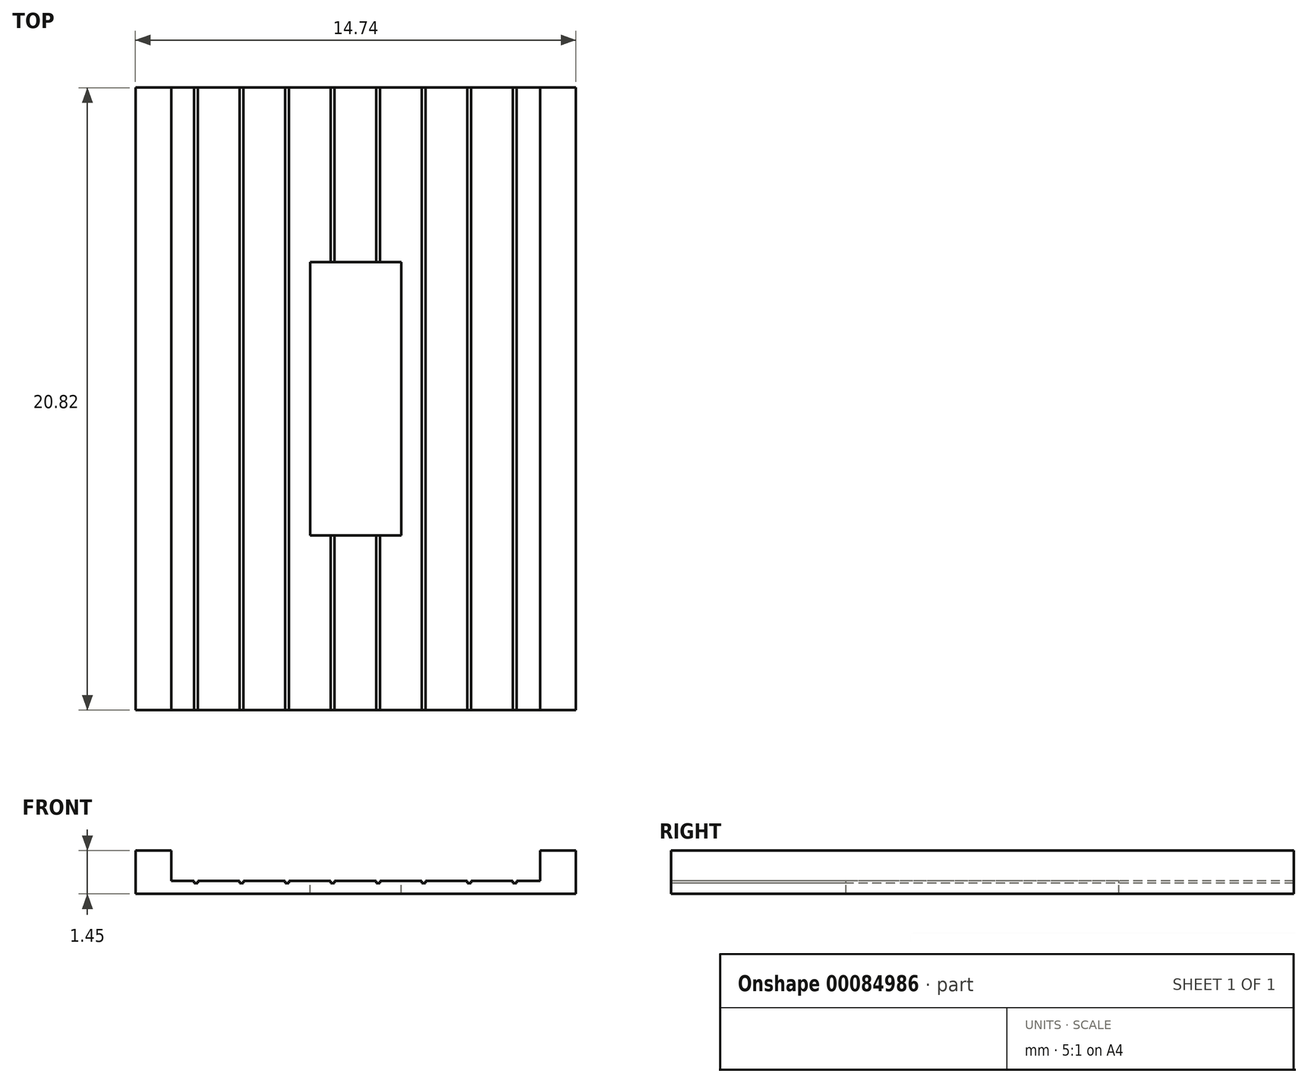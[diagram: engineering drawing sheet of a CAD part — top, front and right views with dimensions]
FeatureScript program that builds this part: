
annotation { "Feature Type Name" : "Feature", "Feature Type Description" : "" }
export const myFeature = defineFeature(function(context is Context, id is Id, definition is map)
    precondition{}
    {
        {
            var Q0;
            Q0=qCreatedBy(makeId("Top.planeOp"),FACE);
            var sketch = newSketch(context, id + "F0", { "sketchPlane" : qUnion([Q0])});
            skLineSegment(sketch, "E0.bottom", {"start": v(-7.37, 10.41) * mm, "end": v(7.37, 10.41) * mm});
            skLineSegment(sketch, "E0.top", {"start": v(-7.37, -10.41) * mm, "end": v(7.37, -10.41) * mm});
            skLineSegment(sketch, "E0.left", {"start": v(-7.37, 10.41) * mm, "end": v(-7.37, -10.41) * mm});
            skLineSegment(sketch, "E0.right", {"start": v(7.37, 10.41) * mm, "end": v(7.37, -10.41) * mm});
            skSolve(sketch);
        }
        {
            var Q0;
            Q0 = qSketchRegion(id + "F0", true);
            var Q1;
            Q1=sQuery(id+"F0.wireOp",EDGE,"E0.bottom");
            var Q2;
            Q2=sQuery(id+"F0.wireOp",EDGE,"E0.top");
            var Q3;
            Q3=sQuery(id+"F0.wireOp",EDGE,"E0.left");
            var Q4;
            Q4=sQuery(id+"F0.wireOp",EDGE,"E0.right");
            extrude(context, id + "F1", {"entities" : qUnion([Q0]), "surfaceEntities" : qUnion([Q1, Q2, Q3, Q4]), "depth" : 0.43 * mm});
        }
        {
            var Q0;
            Q0=makeQuery(id+"F1.opExtrude","CAP_FACE",FACE,{"disambiguationData":[OSD([sQuery(id+"F0.wireOp",EDGE,"E0.bottom"),sQuery(id+"F0.wireOp",EDGE,"E0.top"),sQuery(id+"F0.wireOp",EDGE,"E0.left"),sQuery(id+"F0.wireOp",EDGE,"E0.right")])],"isStart":false});
            var sketch = newSketch(context, id + "F2", { "sketchPlane" : qUnion([Q0])});
            skLineSegment(sketch, "E1.bottom", {"start": v(-5.41, 10.41) * mm, "end": v(-5.28, 10.41) * mm});
            skLineSegment(sketch, "E1.top", {"start": v(-5.41, -10.41) * mm, "end": v(-5.28, -10.41) * mm});
            skLineSegment(sketch, "E1.left", {"start": v(-5.41, 10.41) * mm, "end": v(-5.41, -10.41) * mm});
            skLineSegment(sketch, "E1.right", {"start": v(-5.28, 10.41) * mm, "end": v(-5.28, -10.41) * mm});
            skLineSegment(sketch, "E2.1.0.0", {"start": v(-3.76, 10.41) * mm, "end": v(-3.76, -10.41) * mm});
            skLineSegment(sketch, "E2.1.0.1", {"start": v(-3.89, 10.41) * mm, "end": v(-3.89, -10.41) * mm});
            skLineSegment(sketch, "E2.1.0.2", {"start": v(-3.89, -10.41) * mm, "end": v(-3.76, -10.41) * mm});
            skLineSegment(sketch, "E2.1.0.3", {"start": v(-3.89, 10.41) * mm, "end": v(-3.76, 10.41) * mm});
            skLineSegment(sketch, "E2.2.0.0", {"start": v(-2.24, 10.41) * mm, "end": v(-2.24, -10.41) * mm});
            skLineSegment(sketch, "E2.2.0.1", {"start": v(-2.36, 10.41) * mm, "end": v(-2.36, -10.41) * mm});
            skLineSegment(sketch, "E2.2.0.2", {"start": v(-2.36, -10.41) * mm, "end": v(-2.24, -10.41) * mm});
            skLineSegment(sketch, "E2.2.0.3", {"start": v(-2.36, 10.41) * mm, "end": v(-2.24, 10.41) * mm});
            skLineSegment(sketch, "E2.3.0.0", {"start": v(-0.71, 10.41) * mm, "end": v(-0.71, -10.41) * mm});
            skLineSegment(sketch, "E2.3.0.1", {"start": v(-0.84, 10.41) * mm, "end": v(-0.84, -10.41) * mm});
            skLineSegment(sketch, "E2.3.0.2", {"start": v(-0.84, -10.41) * mm, "end": v(-0.71, -10.41) * mm});
            skLineSegment(sketch, "E2.3.0.3", {"start": v(-0.84, 10.41) * mm, "end": v(-0.71, 10.41) * mm});
            skLineSegment(sketch, "E2.4.0.0", {"start": v(0.81, 10.41) * mm, "end": v(0.81, -10.41) * mm});
            skLineSegment(sketch, "E2.4.0.1", {"start": v(0.69, 10.41) * mm, "end": v(0.69, -10.41) * mm});
            skLineSegment(sketch, "E2.4.0.2", {"start": v(0.69, -10.41) * mm, "end": v(0.81, -10.41) * mm});
            skLineSegment(sketch, "E2.4.0.3", {"start": v(0.69, 10.41) * mm, "end": v(0.81, 10.41) * mm});
            skLineSegment(sketch, "E2.5.0.0", {"start": v(2.34, 10.41) * mm, "end": v(2.34, -10.41) * mm});
            skLineSegment(sketch, "E2.5.0.1", {"start": v(2.2, 10.41) * mm, "end": v(2.2, -10.41) * mm});
            skLineSegment(sketch, "E2.5.0.2", {"start": v(2.2, -10.41) * mm, "end": v(2.34, -10.41) * mm});
            skLineSegment(sketch, "E2.5.0.3", {"start": v(2.2, 10.41) * mm, "end": v(2.34, 10.41) * mm});
            skLineSegment(sketch, "E2.6.0.0", {"start": v(3.86, 10.41) * mm, "end": v(3.86, -10.41) * mm});
            skLineSegment(sketch, "E2.6.0.1", {"start": v(3.73, 10.41) * mm, "end": v(3.73, -10.41) * mm});
            skLineSegment(sketch, "E2.6.0.2", {"start": v(3.73, -10.41) * mm, "end": v(3.86, -10.41) * mm});
            skLineSegment(sketch, "E2.6.0.3", {"start": v(3.73, 10.41) * mm, "end": v(3.86, 10.41) * mm});
            skLineSegment(sketch, "E2.7.0.0", {"start": v(5.38, 10.41) * mm, "end": v(5.38, -10.41) * mm});
            skLineSegment(sketch, "E2.7.0.1", {"start": v(5.26, 10.41) * mm, "end": v(5.26, -10.41) * mm});
            skLineSegment(sketch, "E2.7.0.2", {"start": v(5.26, -10.41) * mm, "end": v(5.38, -10.41) * mm});
            skLineSegment(sketch, "E2.7.0.3", {"start": v(5.26, 10.41) * mm, "end": v(5.38, 10.41) * mm});
            skLineSegment(sketch, "E2.direction1", {"start": v(-5.28, -10.41) * mm, "end": v(-3.76, -10.41) * mm, "construction": true});
            skSolve(sketch);
        }
        {
            var Q0;
            Q0 = qSketchRegion(id + "F2", true);
            extrude(context, id + "F3", {"entities" : qUnion([Q0]), "operationType" : NewBodyOperationType.REMOVE, "oppositeDirection" : true, "depth" : 0.08 * mm});
        }
        {
            var Q0;
            {var subQ0=sQuery(id+"F0.wireOp",EDGE,"E0.bottom");var subQ1=sQuery(id+"F0.wireOp",EDGE,"E0.top");var subQ2=sQuery(id+"F0.wireOp",EDGE,"E0.right");Q0=makeQuery(id+"F3.boolean.opBoolean","SPLIT",FACE,{"disambiguationData":[TD([makeQuery(id+"F1.opExtrude","SWEPT_FACE",FACE,{"disambiguationData":[OSD([subQ2])]})])],"derivedFrom":makeQuery(id+"F1.opExtrude","CAP_FACE",FACE,{"disambiguationData":[OSD([subQ0,subQ1,sQuery(id+"F0.wireOp",EDGE,"E0.left"),subQ2])],"isStart":false})});}
            var sketch = newSketch(context, id + "F4", { "sketchPlane" : qUnion([Q0])});
            skLineSegment(sketch, "E3.bottom", {"start": v(-1.52, 4.57) * mm, "end": v(1.52, 4.57) * mm});
            skLineSegment(sketch, "E3.top", {"start": v(-1.52, -4.57) * mm, "end": v(1.52, -4.57) * mm});
            skLineSegment(sketch, "E3.left", {"start": v(-1.52, 4.57) * mm, "end": v(-1.52, -4.57) * mm});
            skLineSegment(sketch, "E3.right", {"start": v(1.52, 4.57) * mm, "end": v(1.52, -4.57) * mm});
            skSolve(sketch);
        }
        {
            var Q0;
            Q0 = qSketchRegion(id + "F4", true);
            extrude(context, id + "F5", {"entities" : qUnion([Q0]), "operationType" : NewBodyOperationType.REMOVE, "oppositeDirection" : true, "depth" : 25.4 * mm});
        }
        {
            var Q0;
            {var subQ0=sQuery(id+"F0.wireOp",EDGE,"E0.bottom");var subQ1=sQuery(id+"F0.wireOp",EDGE,"E0.top");var subQ2=sQuery(id+"F0.wireOp",EDGE,"E0.left");Q0=makeQuery(id+"F3.boolean.opBoolean","SPLIT",FACE,{"disambiguationData":[TD([makeQuery(id+"F1.opExtrude","SWEPT_FACE",FACE,{"disambiguationData":[OSD([subQ2])]})])],"derivedFrom":makeQuery(id+"F1.opExtrude","CAP_FACE",FACE,{"disambiguationData":[OSD([subQ0,subQ1,subQ2,sQuery(id+"F0.wireOp",EDGE,"E0.right")])],"isStart":false})});}
            var sketch = newSketch(context, id + "F6", { "sketchPlane" : qUnion([Q0])});
            skLineSegment(sketch, "E4.bottom", {"start": v(-7.37, -10.41) * mm, "end": v(-6.17, -10.41) * mm});
            skLineSegment(sketch, "E4.top", {"start": v(-7.37, 10.41) * mm, "end": v(-6.17, 10.41) * mm});
            skLineSegment(sketch, "E4.left", {"start": v(-7.37, -10.41) * mm, "end": v(-7.37, 10.41) * mm});
            skLineSegment(sketch, "E4.right", {"start": v(-6.17, -10.41) * mm, "end": v(-6.17, 10.41) * mm});
            skLineSegment(sketch, "E5.bottom", {"start": v(7.37, 10.41) * mm, "end": v(6.17, 10.41) * mm});
            skLineSegment(sketch, "E5.top", {"start": v(7.37, -10.41) * mm, "end": v(6.17, -10.41) * mm});
            skLineSegment(sketch, "E5.left", {"start": v(7.37, 10.41) * mm, "end": v(7.37, -10.41) * mm});
            skLineSegment(sketch, "E5.right", {"start": v(6.17, 10.41) * mm, "end": v(6.17, -10.41) * mm});
            skSolve(sketch);
        }
        {
            var Q0;
            Q0 = qSketchRegion(id + "F6", true);
            extrude(context, id + "F7", {"entities" : qUnion([Q0]), "operationType" : NewBodyOperationType.ADD, "depth" : 1.02 * mm});
        }
    });
